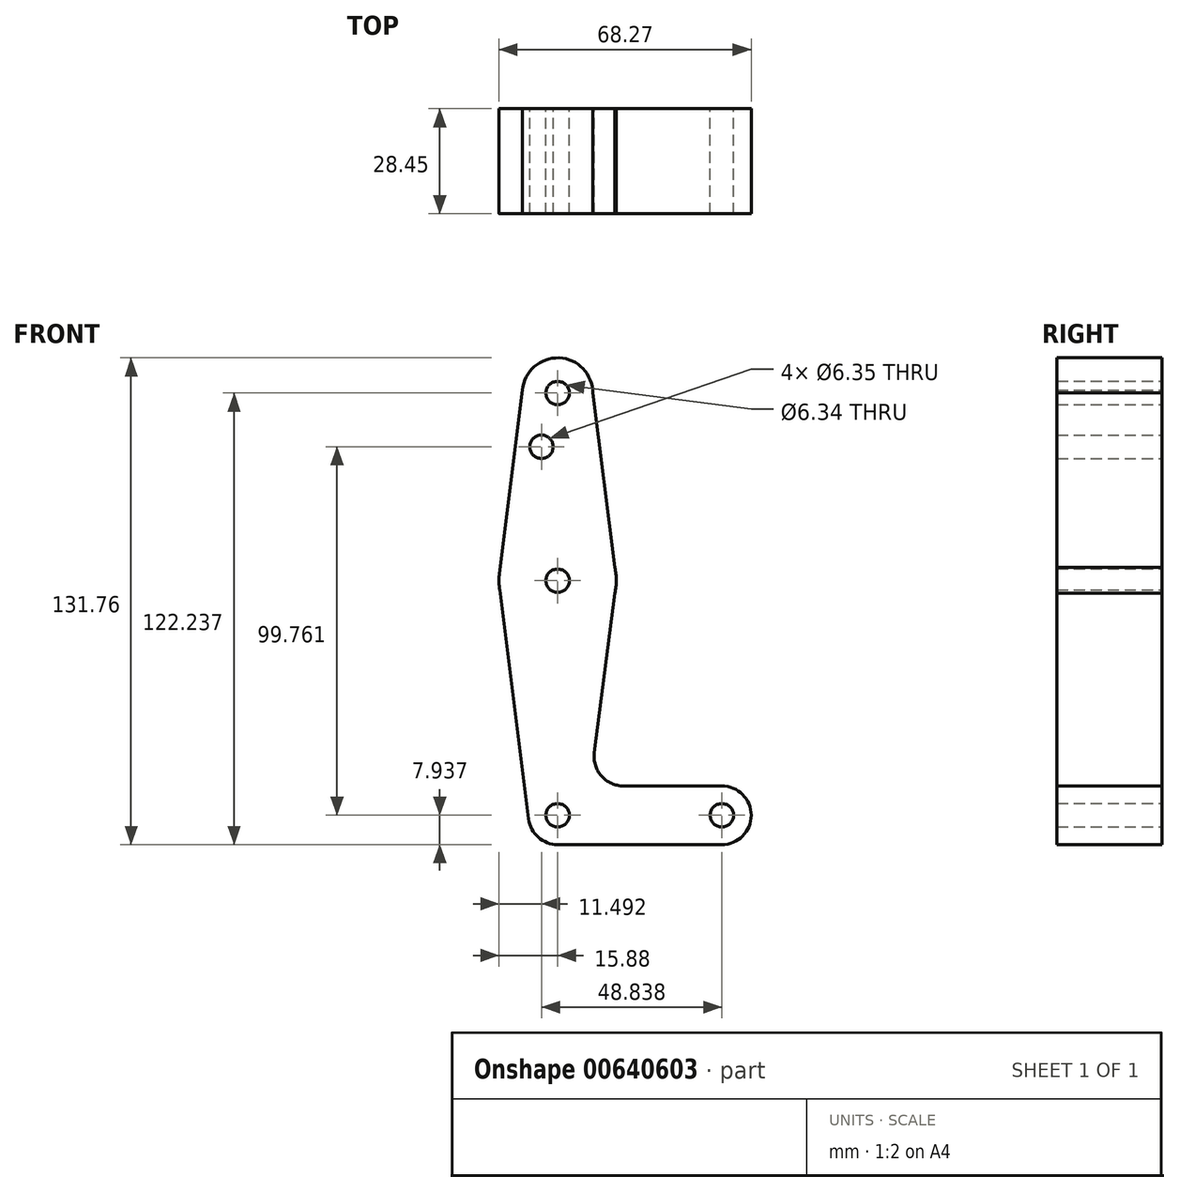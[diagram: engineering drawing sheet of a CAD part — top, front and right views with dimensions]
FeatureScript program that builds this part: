
annotation { "Feature Type Name" : "Feature", "Feature Type Description" : "" }
export const myFeature = defineFeature(function(context is Context, id is Id, definition is map)
    precondition{}
    {
        {
            var Q0;
            Q0=qCreatedBy(makeId("Front.planeOp"),FACE);
            var sketch = newSketch(context, id + "F0", { "sketchPlane" : qUnion([Q0])});
            skCircle(sketch, "E0", {"center": v(0, 58.22) * mm, "radius": 9.53 * mm});
            skCircle(sketch, "E1", {"center": v(0, 7.42) * mm, "radius": 15.88 * mm});
            skCircle(sketch, "E2", {"center": v(44.45, -56.08) * mm, "radius": 7.94 * mm});
            skCircle(sketch, "E3", {"center": v(0, -56.08) * mm, "radius": 7.94 * mm});
            skLineSegment(sketch, "E4", {"start": v(-9.4, 59.8) * mm, "end": v(-15.75, 9.4) * mm});
            skLineSegment(sketch, "E5", {"start": v(-15.8, 5.93) * mm, "end": v(-7.88, -57.07) * mm});
            skLineSegment(sketch, "E6", {"start": v(0, -64.02) * mm, "end": v(44.45, -64.02) * mm});
            skLineSegment(sketch, "E7", {"start": v(9.52, 58.22) * mm, "end": v(15.87, 7.81) * mm});
            skLineSegment(sketch, "E8", {"start": v(15.5, 4.02) * mm, "end": v(9.95, -39.18) * mm});
            skLineSegment(sketch, "E9", {"start": v(44.45, -48.15) * mm, "end": v(17.83, -48.15) * mm});
            skCircle(sketch, "E10", {"center": v(0, 58.22) * mm, "radius": 3.17 * mm});
            skCircle(sketch, "E11", {"center": v(-4.39, 43.68) * mm, "radius": 3.18 * mm});
            skCircle(sketch, "E12", {"center": v(0, 7.42) * mm, "radius": 3.18 * mm});
            skCircle(sketch, "E13", {"center": v(0, -56.08) * mm, "radius": 3.18 * mm});
            skCircle(sketch, "E14", {"center": v(44.45, -56.08) * mm, "radius": 3.18 * mm});
            skPoint(sketch, "E15.newPointA", {"position": v(0, -48.15) * mm});
            skPoint(sketch, "E15.newPointB", {"position": v(7.4, -58.96) * mm});
            skArc(sketch, "E15.filletArc", {"start": v(9.95, -39.18) * mm, "mid": v(11.86, -45.45) * mm, "end": v(17.83, -48.15) * mm});
            skCircle(sketch, "E16", {"center": v(0, -56.08) * mm, "radius": 1.2 * mm});
            skCircle(sketch, "E17", {"center": v(0, -56.08) * mm, "radius": 1.62 * mm});
            skSolve(sketch);
        }
        {
            var Q0;
            Q0 = qSketchRegion(id + "F0", true);
            extrude(context, id + "F1", {"entities" : qUnion([Q0]), "depth" : 3.05 * mm, "offsetDistance" : 25.4 * mm});
        }
        {
            var Q0;
            Q0 = qSketchRegion(id + "F0", true);
            extrude(context, id + "F2", {"entities" : qUnion([Q0]), "operationType" : NewBodyOperationType.ADD, "depth" : 3.05 * mm, "offsetDistance" : 25.4 * mm});
        }
        {
            var Q0;
            Q0 = qSketchRegion(id + "F0", true);
            extrude(context, id + "F3", {"entities" : qUnion([Q0]), "operationType" : NewBodyOperationType.ADD, "depth" : 3.05 * mm, "offsetDistance" : 25.4 * mm});
        }
        {
            var Q0;
            Q0 = qSketchRegion(id + "F0", true);
            var Q1;
            Q1=makeQuery(id+"F1.opExtrude","CAP_FACE",FACE,{"disambiguationData":[OSD([sQuery(id+"F0.wireOp",EDGE,"E0"),sQuery(id+"F0.wireOp",EDGE,"E1"),sQuery(id+"F0.wireOp",EDGE,"E2"),sQuery(id+"F0.wireOp",EDGE,"E3"),sQuery(id+"F0.wireOp",EDGE,"E4"),sQuery(id+"F0.wireOp",EDGE,"E5"),sQuery(id+"F0.wireOp",EDGE,"E6"),sQuery(id+"F0.wireOp",EDGE,"E7"),sQuery(id+"F0.wireOp",EDGE,"E8"),sQuery(id+"F0.wireOp",EDGE,"E9"),sQuery(id+"F0.wireOp",EDGE,"E10"),sQuery(id+"F0.wireOp",EDGE,"E11"),sQuery(id+"F0.wireOp",EDGE,"E12"),sQuery(id+"F0.wireOp",EDGE,"E13"),sQuery(id+"F0.wireOp",EDGE,"E14"),sQuery(id+"F0.wireOp",EDGE,"E15.filletArc")])],"isStart":false});
            extrude(context, id + "F4", {"entities" : qUnion([Q0, Q1]), "operationType" : NewBodyOperationType.ADD, "depth" : 25.4 * mm, "offsetDistance" : 25.4 * mm});
        }
    });
